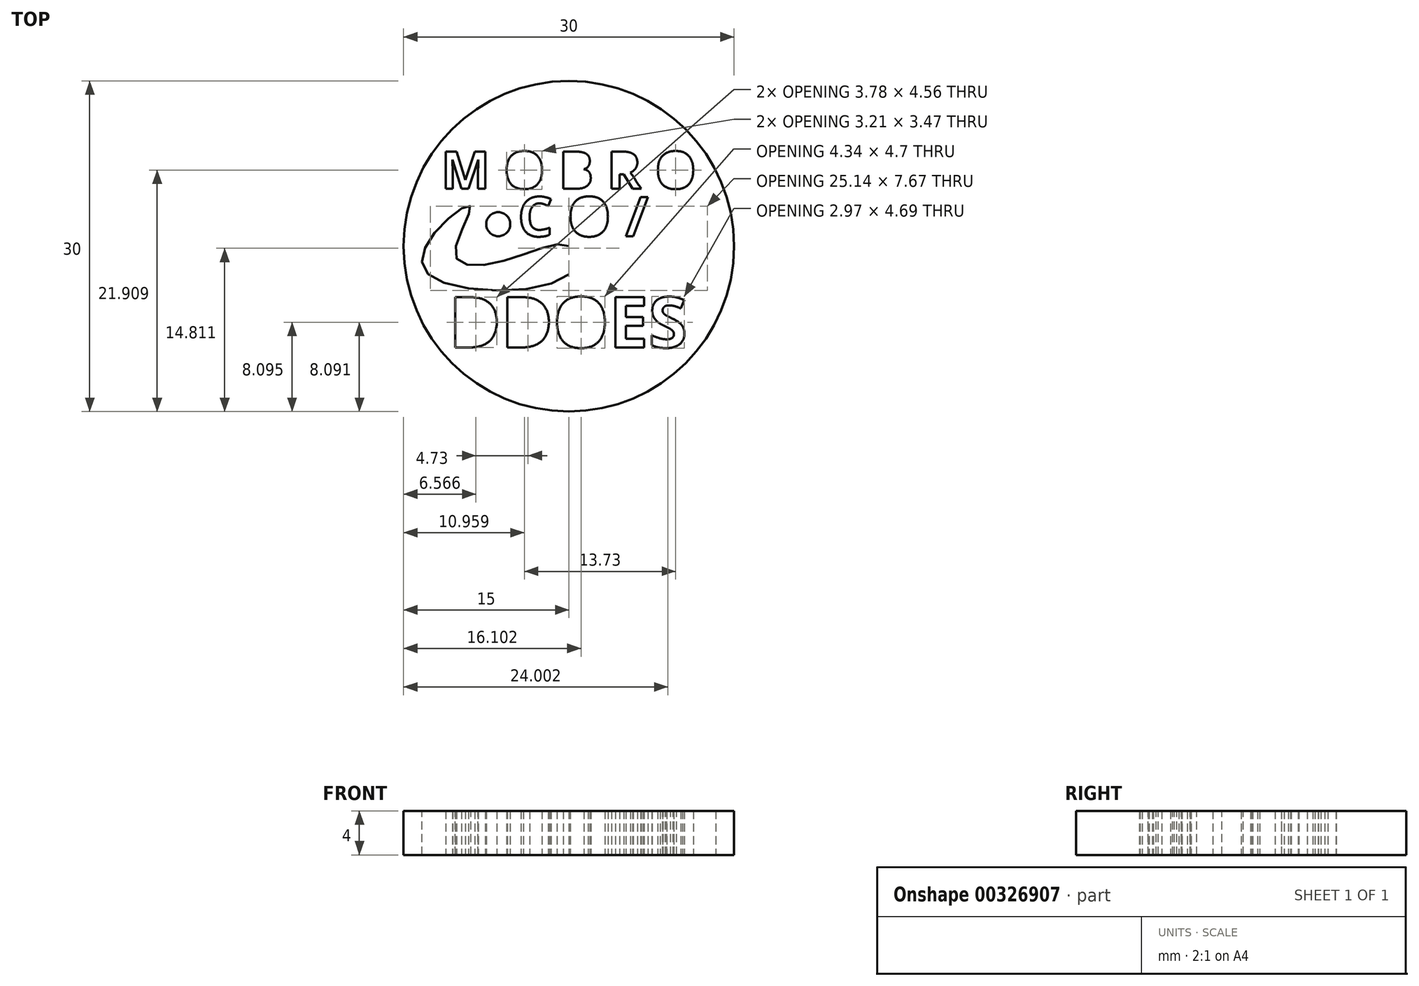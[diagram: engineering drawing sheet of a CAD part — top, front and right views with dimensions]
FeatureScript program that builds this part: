
annotation { "Feature Type Name" : "Feature", "Feature Type Description" : "" }
export const myFeature = defineFeature(function(context is Context, id is Id, definition is map)
    precondition{}
    {
        {
            var Q0;
            Q0=qCreatedBy(makeId("Top.planeOp"),FACE);
            var sketch = newSketch(context, id + "F0", { "sketchPlane" : qUnion([Q0])});
            skCircle(sketch, "E0", {"center": v(0, 0) * mm, "radius": 15 * mm});
            skLineSegment(sketch, "E1", {"start": v(0, 0) * mm, "end": v(0, -2.56) * mm});
            skFitSpline(sketch, "E2", {"points": [v(0, 0) * mm, v(5.77, -1.3) * mm, v(10.3, -0.79) * mm, v(8.92, 3.59) * mm, v(12.37, 0.98) * mm, v(12.44, -2.8) * mm, v(0, -2.56) * mm, v(0, 0) * mm]});
            skFitSpline(sketch, "E3.MirrorC", {"points": [v(0, 0) * mm, v(-5.77, -1.3) * mm, v(-10.3, -0.79) * mm, v(-8.92, 3.59) * mm, v(-12.37, 0.98) * mm, v(-12.44, -2.8) * mm, v(0, -2.56) * mm, v(0, 0) * mm]});
            skText(sketch, "E4", { "text": "M O B R O", "fontName": "OpenSans-Bold.ttf"});
            skText(sketch, "E5", { "text": "DDOES", "fontName": "OpenSans-Bold.ttf"});
            skText(sketch, "E6", { "text": "C O /", "fontName": "OpenSans-Bold.ttf"});
            skCircle(sketch, "E7", {"center": v(-6.4, 2) * mm, "radius": 1.1 * mm});
            skLineSegment(sketch, "E8", {"start": v(-4.63, 0.9) * mm, "end": v(-9.49, 0.9) * mm, "construction": true});
            skPoint(sketch, "E9", {"position": v(-1.08, 0.63) * mm});
            skLineSegment(sketch, "E10", {"start": v(7.5, 0.35) * mm, "end": v(0, 0.35) * mm, "construction": true});
            const initialGuessF0  = {"E4": [-0.0116, 0.00522, 1, 0, 0.0034], "E5": [-0.0109, -0.00919, 1, 0, 0.0046], "E6": [-0.00463, 0.0009, 1, 0, 0.0036]};
            skSetInitialGuess(sketch, initialGuessF0);
            skSolve(sketch);
        }
        {
            var Q0;
            Q0 = qSketchRegion(id + "F0", true);
            extrude(context, id + "F1", {"entities" : qUnion([Q0]), "depth" : 4 * mm});
        }
    });
